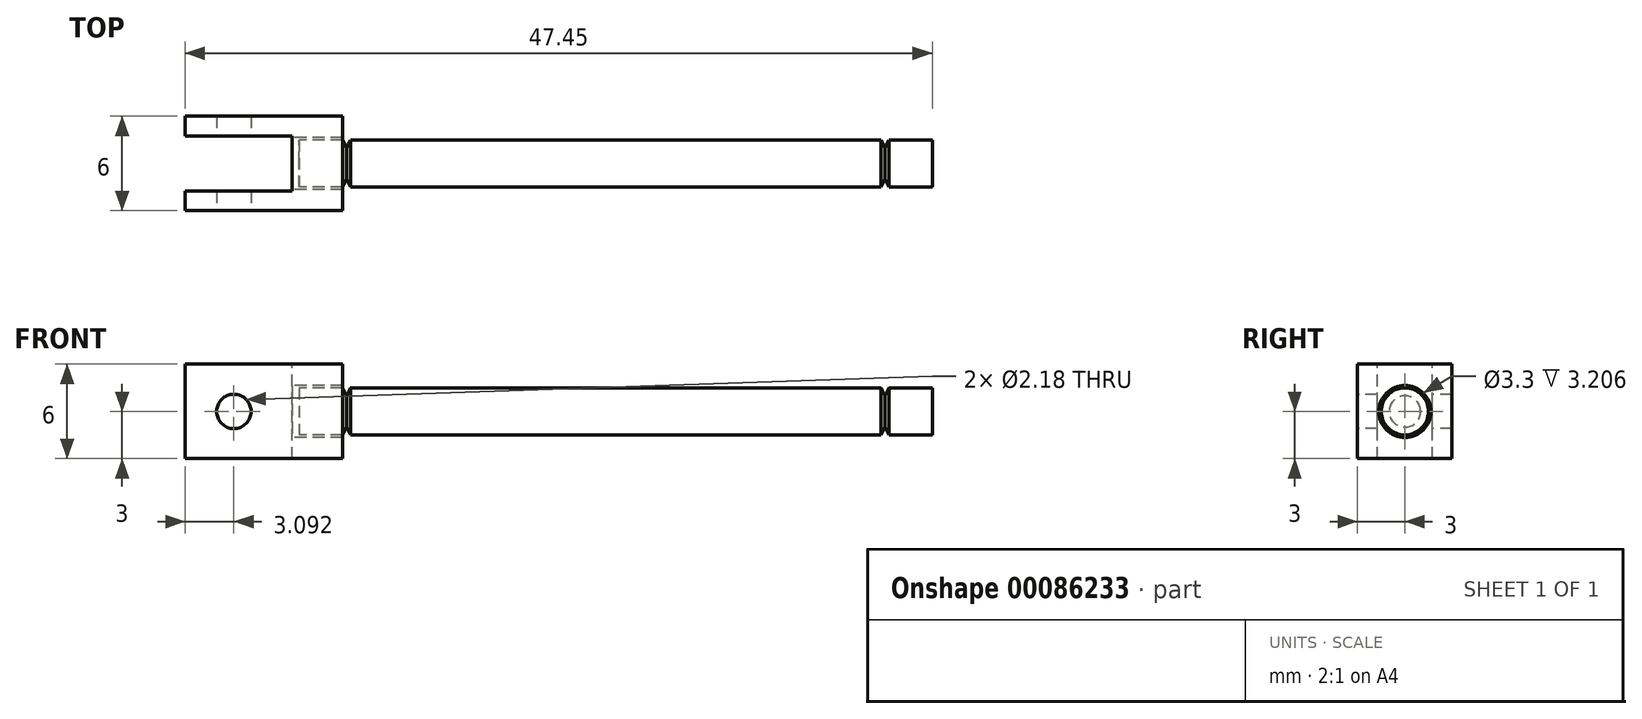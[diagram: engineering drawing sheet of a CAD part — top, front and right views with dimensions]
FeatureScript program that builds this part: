
annotation { "Feature Type Name" : "Feature", "Feature Type Description" : "" }
export const myFeature = defineFeature(function(context is Context, id is Id, definition is map)
    precondition{}
    {
        {
            var Q0;
            Q0=qCreatedBy(makeId("Front.planeOp"),FACE);
            var sketch = newSketch(context, id + "F0", { "sketchPlane" : qUnion([Q0])});
            skLineSegment(sketch, "E0", {"start": v(-40.2, 1.5) * mm, "end": v(-37.45, 1.5) * mm});
            skLineSegment(sketch, "E1", {"start": v(-3.25, 1.5) * mm, "end": v(-3, 1) * mm});
            skLineSegment(sketch, "E2", {"start": v(-3, 1) * mm, "end": v(-2.75, 1.5) * mm});
            skLineSegment(sketch, "E3", {"start": v(-2.75, 1.5) * mm, "end": v(0, 1.5) * mm});
            skLineSegment(sketch, "E4", {"start": v(0, 1.5) * mm, "end": v(0, 0) * mm});
            skLineSegment(sketch, "E5", {"start": v(-40.2, 1.5) * mm, "end": v(-40.2, 0) * mm});
            skLineSegment(sketch, "E6", {"start": v(-40.2, 0) * mm, "end": v(0, 0) * mm});
            skLineSegment(sketch, "E7", {"start": v(-37.45, 1.5) * mm, "end": v(-37.2, 1) * mm});
            skLineSegment(sketch, "E8", {"start": v(-37.2, 1) * mm, "end": v(-36.95, 1.5) * mm});
            skLineSegment(sketch, "E9.trimOffspring", {"start": v(-36.95, 1.5) * mm, "end": v(-3.25, 1.5) * mm});
            skSolve(sketch);
        }
        {
            var Q0;
            Q0=makeQuery(id+"F0.imprint","IMPRINT",FACE,{"disambiguationData":[TD([[makeQuery(id+"F0.imprint","IMPRINT",EDGE,{"derivedFrom":sQuery(id+"F0.wireOp",EDGE,"E0")}),-1.0]])]});
            var Q1;
            Q1=sQuery(id+"F0.wireOp",EDGE,"E6");
            revolve(context, id + "F1", {"entities" : qUnion([Q0]), "axis" : qUnion([Q1]), "revolveType" : RevolveType.FULL});
        }
        {
            var Q0;
            Q0=qCreatedBy(makeId("Top.planeOp"),FACE);
            var sketch = newSketch(context, id + "F2", { "sketchPlane" : qUnion([Q0])});
            skLineSegment(sketch, "E10.bottom", {"start": v(-47.45, 3) * mm, "end": v(-37.45, 3) * mm});
            skLineSegment(sketch, "E10.top", {"start": v(-47.45, -3) * mm, "end": v(-37.45, -3) * mm});
            skLineSegment(sketch, "E10.left", {"start": v(-47.45, 3) * mm, "end": v(-47.45, -3) * mm});
            skLineSegment(sketch, "E10.right", {"start": v(-37.45, 3) * mm, "end": v(-37.45, -3) * mm});
            skPoint(sketch, "E11", {"position": v(-37.45, 0) * mm});
            skLineSegment(sketch, "E12.0", {"start": v(-36.95, -1.5) * mm, "end": v(-36.95, 1.5) * mm, "construction": true});
            skSolve(sketch);
        }
        {
            var Q0;
            Q0=makeQuery(id+"F2.imprint","IMPRINT",FACE,{"disambiguationData":[TD([[makeQuery(id+"F2.imprint","IMPRINT",EDGE,{"derivedFrom":sQuery(id+"F2.wireOp",EDGE,"E10.bottom")}),-1.0]])]});
            extrude(context, id + "F3", {"entities" : qUnion([Q0]), "depth" : 6 * mm, "offsetDistance" : 25 * mm, "symmetric" : true});
        }
        {
            var Q0;
            Q0=makeQuery(id+"F3.opExtrude","SWEPT_FACE",FACE,{"disambiguationData":[OSD([sQuery(id+"F2.wireOp",EDGE,"E10.right")])]});
            var sketch = newSketch(context, id + "F4", { "sketchPlane" : qUnion([Q0])});
            skPoint(sketch, "E13", {"position": v(0, 0) * mm});
            skSolve(sketch);
        }
        {
            var Q0;
            Q0=sQuery(id+"F4.wireOp",VERTEX,"E13");
            var Q1;
            Q1=makeQuery(id+"F3.opExtrude","SWEPT_BODY",BODY,{"disambiguationData":[OSD([sQuery(id+"F2.wireOp",EDGE,"E10.bottom"),sQuery(id+"F2.wireOp",EDGE,"E10.top"),sQuery(id+"F2.wireOp",EDGE,"E10.left"),sQuery(id+"F2.wireOp",EDGE,"E10.right")])]});
            hole(context, id + "F5", {"style" : HoleStyle.SIMPLE, "endStyle" : HoleEndStyle.BLIND, "standardTappedOrClearance" : lookupTablePath({ "standard" : "ISO", "fit" : "Normal", "size" : "M3", "type" : "Clearance" }), "standardBlindInLast" : lookupTablePath({ "fit" : "Standard", "standard" : "ISO", "size" : "M3", "type" : "Clearance" }), "holeDiameter" : 3.3 * mm, "majorDiameter" : 3 * mm, "holeDepth" : 4 * mm, "isTappedThrough" : true, "tappedDepth" : 3.47 * mm, "tapClearance" : 1, "locations" : qUnion([Q0]), "scope" : qUnion([Q1])});
        }
        {
            var Q0;
            Q0=makeQuery(id+"F3.opExtrude","SWEPT_FACE",FACE,{"disambiguationData":[OSD([sQuery(id+"F2.wireOp",EDGE,"E10.top")])]});
            var sketch = newSketch(context, id + "F6", { "sketchPlane" : qUnion([Q0])});
            skCircle(sketch, "E14", {"center": v(-44.36, 0) * mm, "radius": 1.1 * mm});
            skLineSegment(sketch, "E15.0", {"start": v(0, -1.5) * mm, "end": v(0, 1.5) * mm, "construction": true});
            skLineSegment(sketch, "E16", {"start": v(0, 0) * mm, "end": v(-44.36, 0) * mm, "construction": true});
            skLineSegment(sketch, "E17", {"start": v(-45.45, 3) * mm, "end": v(-45.45, -3) * mm, "construction": true});
            skSolve(sketch);
        }
        {
            var Q0;
            Q0=makeQuery(id+"F6.imprint","IMPRINT",FACE,{"disambiguationData":[TD([[makeQuery(id+"F6.imprint","IMPRINT",EDGE,{"derivedFrom":sQuery(id+"F6.wireOp",EDGE,"E14")}),1.0]])]});
            extrude(context, id + "F7", {"entities" : qUnion([Q0]), "operationType" : NewBodyOperationType.REMOVE, "endBound" : BoundingType.THROUGH_ALL, "oppositeDirection" : true, "depth" : 25 * mm, "offsetDistance" : 25 * mm});
        }
        {
            var Q0;
            Q0=makeQuery(id+"F3.opExtrude","CAP_FACE",FACE,{"disambiguationData":[OSD([sQuery(id+"F2.wireOp",EDGE,"E10.bottom"),sQuery(id+"F2.wireOp",EDGE,"E10.top"),sQuery(id+"F2.wireOp",EDGE,"E10.left"),sQuery(id+"F2.wireOp",EDGE,"E10.right")])],"isStart":false});
            var sketch = newSketch(context, id + "F8", { "sketchPlane" : qUnion([Q0])});
            skLineSegment(sketch, "E18.bottom", {"start": v(-47.45, 1.75) * mm, "end": v(-40.66, 1.75) * mm});
            skLineSegment(sketch, "E18.top", {"start": v(-47.45, -1.75) * mm, "end": v(-40.66, -1.75) * mm});
            skLineSegment(sketch, "E18.left", {"start": v(-47.45, 1.75) * mm, "end": v(-47.45, 0) * mm});
            skLineSegment(sketch, "E18.right", {"start": v(-40.66, 1.75) * mm, "end": v(-40.66, -1.75) * mm});
            skPoint(sketch, "E19", {"position": v(-47.45, 0) * mm});
            skLineSegment(sketch, "E20", {"start": v(-47.45, 0) * mm, "end": v(-47.45, -1.75) * mm});
            skSolve(sketch);
        }
        {
            var Q0;
            Q0=makeQuery(id+"F8.imprint","IMPRINT",FACE,{"disambiguationData":[TD([[makeQuery(id+"F8.imprint","IMPRINT",EDGE,{"derivedFrom":sQuery(id+"F8.wireOp",EDGE,"E18.bottom")}),-1.0]])]});
            extrude(context, id + "F9", {"entities" : qUnion([Q0]), "operationType" : NewBodyOperationType.REMOVE, "endBound" : BoundingType.THROUGH_ALL, "oppositeDirection" : true, "depth" : 25 * mm, "offsetDistance" : 25 * mm});
        }
    });
